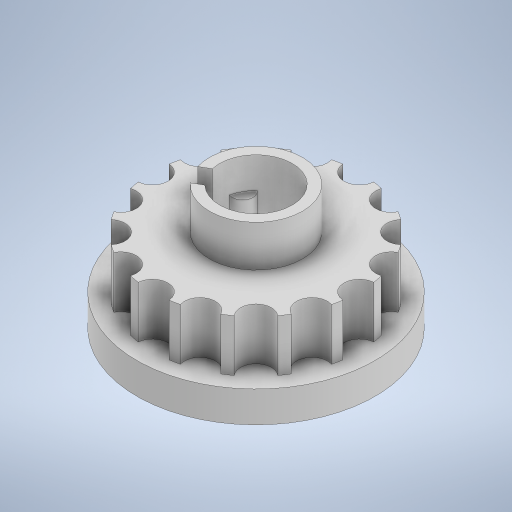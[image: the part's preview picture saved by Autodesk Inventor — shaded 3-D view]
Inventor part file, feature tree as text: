
AUTODESK INVENTOR PART (.ipt)
format: ipt  version: 2023 (Build 270158000, 158)  size: 384,512 bytes
history: native  units: mm
features: extrude x6, sketch x6, other x1
ambient origin geometry x8: Origin, YZ Plane, XZ Plane, XY Plane, X Axis, Y Axis, Z Axis, Center Point
bodies: Body1 (feature_tree)
feature tree (13):
  other  "Твердое тело1"
  extrude  "Выдавливание1"  Depth=23.0mm
  extrude  "Выдавливание2"  Depth=17.0mm
  extrude  "Выдавливание3"  Depth=3.0mm TaperAngle=0.0deg
  extrude  "Выдавливание4"  Depth=20.0mm
  extrude  "Выдавливание5"  Depth=3.0mm
  extrude  "Выдавливание6"  Depth=160.0mm TaperAngle=360.0deg
  sketch  "Эскиз1"
  sketch  "Эскиз2"
  sketch  "Эскиз3"
  sketch  "Эскиз4"
  sketch  "Эскиз5"
  sketch  "Эскиз6"
